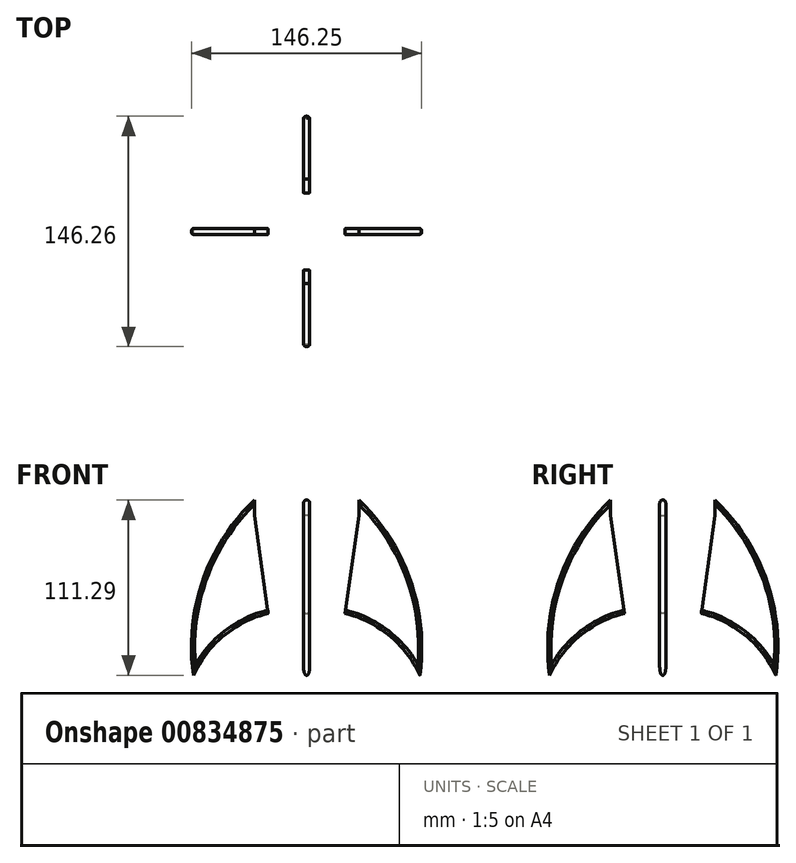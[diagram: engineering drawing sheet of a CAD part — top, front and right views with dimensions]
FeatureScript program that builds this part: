
annotation { "Feature Type Name" : "Feature", "Feature Type Description" : "" }
export const myFeature = defineFeature(function(context is Context, id is Id, definition is map)
    precondition{}
    {
        {
            var Q0;
            Q0=qCreatedBy(makeId("Front.planeOp"),FACE);
            var sketch = newSketch(context, id + "F0", { "sketchPlane" : qUnion([Q0])});
            skLineSegment(sketch, "E0", {"start": v(0, 1.98) * mm, "end": v(0, 124.8) * mm, "construction": true});
            skLineSegment(sketch, "E1.bottom", {"start": v(-9, 31.24) * mm, "end": v(9, 31.24) * mm, "construction": true});
            skLineSegment(sketch, "E1.top", {"start": v(-9, 101.24) * mm, "end": v(9, 101.24) * mm, "construction": true});
            skLineSegment(sketch, "E1.left", {"start": v(-9, 31.24) * mm, "end": v(-9, 101.24) * mm, "construction": true});
            skLineSegment(sketch, "E1.right", {"start": v(9, 31.24) * mm, "end": v(9, 101.24) * mm, "construction": true});
            skSolve(sketch);
        }
        {
            var Q0;
            Q0=qCreatedBy(makeId("Front.planeOp"),FACE);
            var sketch = newSketch(context, id + "F1", { "sketchPlane" : qUnion([Q0])});
            skLineSegment(sketch, "E2.MirrorCS", {"start": v(9.15, 101.26) * mm, "end": v(9.15, 33.17) * mm});
            skLineSegment(sketch, "E3.MirrorCS", {"start": v(33.01, 101.3) * mm, "end": v(23.86, 34.74) * mm});
            skLineSegment(sketch, "E4.MirrorCS", {"start": v(32, 101.3) * mm, "end": v(9.15, 101.26) * mm});
            skLineSegment(sketch, "E5.MirrorCS", {"start": v(32, 101.3) * mm, "end": v(32, 111.3) * mm});
            skLineSegment(sketch, "E6.MirrorCS", {"start": v(33.01, 111.3) * mm, "end": v(33.01, 101.3) * mm});
            skLineSegment(sketch, "E7.MirrorCS", {"start": v(32, 111.3) * mm, "end": v(33.01, 111.3) * mm});
            skLineSegment(sketch, "E8.MirrorCS", {"start": v(19.69, 21.09) * mm, "end": v(19.69, 34.74) * mm});
            skLineSegment(sketch, "E9.MirrorCS", {"start": v(19.69, 34.74) * mm, "end": v(23.86, 34.74) * mm});
            skLineSegment(sketch, "E10.MirrorCS", {"start": v(9.15, 33.17) * mm, "end": v(11.05, 33.17) * mm});
            skLineSegment(sketch, "E11.MirrorCS", {"start": v(11.05, 33.17) * mm, "end": v(11.05, 30.73) * mm});
            skLineSegment(sketch, "E12.MirrorCS", {"start": v(11.05, 30.73) * mm, "end": v(18.59, 21.09) * mm});
            skLineSegment(sketch, "E13.MirrorCS", {"start": v(18.59, 21.09) * mm, "end": v(19.69, 21.09) * mm});
            skLineSegment(sketch, "E14", {"start": v(12.5, 94.18) * mm, "end": v(28.58, 94.18) * mm});
            skLineSegment(sketch, "E15", {"start": v(28.58, 94.18) * mm, "end": v(21.03, 39.29) * mm});
            skLineSegment(sketch, "E16", {"start": v(21.03, 39.29) * mm, "end": v(12.3, 39.29) * mm});
            skLineSegment(sketch, "E17", {"start": v(12.3, 39.29) * mm, "end": v(12.5, 94.18) * mm});
            skSolve(sketch);
        }
        {
            var Q0;
            Q0=qCreatedBy(makeId("Front.planeOp"),FACE);
            var sketch = newSketch(context, id + "F2", { "sketchPlane" : qUnion([Q0])});
            skLineSegment(sketch, "E18", {"start": v(-19.33, 101.39) * mm, "end": v(-19.33, 106.39) * mm});
            skLineSegment(sketch, "E19", {"start": v(-19.33, 106.39) * mm, "end": v(-9.53, 106.39) * mm});
            skLineSegment(sketch, "E20", {"start": v(-9.53, 106.39) * mm, "end": v(-9.53, 166) * mm});
            skLineSegment(sketch, "E21", {"start": v(-9.53, 166) * mm, "end": v(-19.33, 166) * mm});
            skLineSegment(sketch, "E22", {"start": v(-19.33, 166) * mm, "end": v(-19.33, 172.66) * mm});
            skLineSegment(sketch, "E23", {"start": v(-19.33, 172.66) * mm, "end": v(-7.98, 172.66) * mm});
            skLineSegment(sketch, "E24", {"start": v(-7.98, 172.66) * mm, "end": v(-7.98, 171.53) * mm});
            skLineSegment(sketch, "E25", {"start": v(-7.98, 171.53) * mm, "end": v(-9, 171.53) * mm});
            skLineSegment(sketch, "E26", {"start": v(-9, 171.53) * mm, "end": v(-9, 104.37) * mm});
            skArc(sketch, "E27", {"start": v(-9, 104.37) * mm, "mid": v(-10.81, 103.2) * mm, "end": v(-11.96, 101.39) * mm});
            skLineSegment(sketch, "E28", {"start": v(-11.96, 101.39) * mm, "end": v(-19.33, 101.39) * mm});
            skSolve(sketch);
        }
        {
            var Q0;
            Q0=sQuery(id+"F1.wireOp",EDGE,"E2.MirrorCS");
            var Q1;
            Q1=sQuery(id+"F1.wireOp",EDGE,"E4.MirrorCS");
            var Q2;
            Q2=sQuery(id+"F1.wireOp",EDGE,"E6.MirrorCS");
            var Q3;
            Q3=sQuery(id+"F1.wireOp",EDGE,"E3.MirrorCS");
            var Q4;
            Q4=sQuery(id+"F1.wireOp",EDGE,"E5.MirrorCS");
            var Q5;
            Q5=sQuery(id+"F1.wireOp",EDGE,"E9.MirrorCS");
            var Q6;
            Q6=sQuery(id+"F1.wireOp",EDGE,"E11.MirrorCS");
            var Q7;
            Q7=sQuery(id+"F1.wireOp",EDGE,"E7.MirrorCS");
            var Q8;
            Q8=sQuery(id+"F1.wireOp",EDGE,"E10.MirrorCS");
            var Q9;
            Q9=sQuery(id+"F1.wireOp",EDGE,"E8.MirrorCS");
            var Q10;
            Q10=sQuery(id+"F1.wireOp",EDGE,"E12.MirrorCS");
            var Q11;
            Q11=sQuery(id+"F1.wireOp",EDGE,"E13.MirrorCS");
            var Q12;
            Q12 = qConstructionFilter(qBodyType(qCreatedBy(id + "F2" ,EDGE), BodyType.WIRE), ConstructionObject.NO);
            var Q13;
            Q13=sQuery(id+"F0.wireOp",EDGE,"E0");
            revolve(context, id + "F3", {"bodyType" : ToolBodyType.SURFACE, "surfaceOperationType" : NewSurfaceOperationType.NEW, "surfaceEntities" : qUnion([Q0, Q1, Q2, Q3, Q4, Q5, Q6, Q7, Q8, Q9, Q10, Q11, Q12]), "axis" : qUnion([Q13]), "revolveType" : RevolveType.FULL});
        }
        {
            var Q0;
            Q0=makeQuery(id+"F3.opRevolve","SWEPT_EDGE",EDGE,{"disambiguationData":[OSD([sQuery(id+"F1.wireOp",VERTEX,"E4.MirrorCS.end")])]});
            var Q1;
            Q1=makeQuery(id+"F3.opRevolve","SWEPT_EDGE",EDGE,{"disambiguationData":[OSD([sQuery(id+"F1.wireOp",VERTEX,"E13.MirrorCS.end")])]});
            var Q2;
            Q2=makeQuery(id+"F3.opRevolve","SWEPT_EDGE",EDGE,{"disambiguationData":[OSD([sQuery(id+"F1.wireOp",VERTEX,"E10.MirrorCS.start")])]});
            fillet(context, id + "F4", {"entities" : qUnion([Q0, Q1, Q2]), "radius" : 5 * mm, "tangentPropagation" : true, "allowEdgeOverflow" : false});
        }
        {
            var Q0;
            Q0=qCreatedBy(makeId("Front.planeOp"),FACE);
            var sketch = newSketch(context, id + "F5", { "sketchPlane" : qUnion([Q0])});
            skArc(sketch, "E29", {"start": v(-24.4, 39.36) * mm, "mid": v(-52.64, 25.1) * mm, "end": v(-71.9, 0) * mm});
            skArc(sketch, "E30", {"start": v(-33.16, 111.3) * mm, "mid": v(-65.94, 60.31) * mm, "end": v(-71.9, 0) * mm});
            skLineSegment(sketch, "E31", {"start": v(-33.16, 111.3) * mm, "end": v(-33.16, 101.44) * mm});
            skLineSegment(sketch, "E32", {"start": v(-33.16, 101.44) * mm, "end": v(-24.4, 39.36) * mm});
            skArc(sketch, "E33.MirrorCS", {"start": v(33.16, 111.3) * mm, "mid": v(65.94, 60.31) * mm, "end": v(71.9, 0) * mm});
            skArc(sketch, "E34.MirrorCS", {"start": v(24.4, 39.36) * mm, "mid": v(52.64, 25.1) * mm, "end": v(71.9, 0) * mm});
            skLineSegment(sketch, "E35.MirrorCS", {"start": v(33.16, 101.44) * mm, "end": v(24.4, 39.36) * mm});
            skLineSegment(sketch, "E36.MirrorCS", {"start": v(33.16, 111.3) * mm, "end": v(33.16, 101.44) * mm});
            skSolve(sketch);
        }
        {
            var Q0;
            Q0=qSketchRegion(id+"F5",true);
            extrude(context, id + "F6", {"entities" : qUnion([Q0]), "depth" : 2 * mm, "offsetDistance" : 25 * mm, "hasSecondDirection" : true, "secondDirectionOppositeDirection" : true, "secondDirectionDepth" : 2 * mm});
        }
        {
            var Q0;
            Q0=qCreatedBy(makeId("Right.planeOp"),FACE);
            var sketch = newSketch(context, id + "F7", { "sketchPlane" : qUnion([Q0])});
            skArc(sketch, "E37", {"start": v(-24.36, 39.36) * mm, "mid": v(-52.6, 25.1) * mm, "end": v(-71.86, 0) * mm});
            skArc(sketch, "E38", {"start": v(-33.12, 111.3) * mm, "mid": v(-65.9, 60.31) * mm, "end": v(-71.86, 0) * mm});
            skLineSegment(sketch, "E39", {"start": v(-33.12, 111.3) * mm, "end": v(-33.12, 101.44) * mm});
            skLineSegment(sketch, "E40", {"start": v(-33.12, 101.44) * mm, "end": v(-24.36, 39.36) * mm});
            skArc(sketch, "E41.MirrorCS", {"start": v(33.2, 111.3) * mm, "mid": v(65.98, 60.31) * mm, "end": v(71.94, 0) * mm});
            skArc(sketch, "E42.MirrorCS", {"start": v(24.44, 39.36) * mm, "mid": v(52.69, 25.1) * mm, "end": v(71.94, 0) * mm});
            skLineSegment(sketch, "E43.MirrorCS", {"start": v(33.2, 101.44) * mm, "end": v(24.44, 39.36) * mm});
            skLineSegment(sketch, "E44.MirrorCS", {"start": v(33.2, 111.3) * mm, "end": v(33.2, 101.44) * mm});
            skSolve(sketch);
        }
        {
            var Q0;
            Q0=qSketchRegion(id+"F7",true);
            extrude(context, id + "F8", {"entities" : qUnion([Q0]), "depth" : 2 * mm, "offsetDistance" : 25 * mm, "hasSecondDirection" : true, "secondDirectionOppositeDirection" : true, "secondDirectionDepth" : 2 * mm});
        }
        {
            var Q0;
            Q0=makeQuery(id+"F6.opExtrude","CAP_EDGE",EDGE,{"disambiguationData":[OSD([sQuery(id+"F5.wireOp",EDGE,"E33.MirrorCS")])],"isStart":false});
            var Q1;
            Q1=makeQuery(id+"F6.opExtrude","CAP_EDGE",EDGE,{"disambiguationData":[OSD([sQuery(id+"F5.wireOp",EDGE,"E33.MirrorCS")])],"isStart":true});
            var Q2;
            Q2=makeQuery(id+"F6.opExtrude","CAP_EDGE",EDGE,{"disambiguationData":[OSD([sQuery(id+"F5.wireOp",EDGE,"E34.MirrorCS")])],"isStart":false});
            var Q3;
            Q3=makeQuery(id+"F6.opExtrude","CAP_EDGE",EDGE,{"disambiguationData":[OSD([sQuery(id+"F5.wireOp",EDGE,"E34.MirrorCS")])],"isStart":true});
            var Q4;
            Q4=makeQuery(id+"F6.opExtrude","CAP_EDGE",EDGE,{"disambiguationData":[OSD([sQuery(id+"F5.wireOp",EDGE,"E30")])],"isStart":false});
            var Q5;
            Q5=makeQuery(id+"F6.opExtrude","CAP_EDGE",EDGE,{"disambiguationData":[OSD([sQuery(id+"F5.wireOp",EDGE,"E30")])],"isStart":true});
            var Q6;
            Q6=makeQuery(id+"F6.opExtrude","CAP_EDGE",EDGE,{"disambiguationData":[OSD([sQuery(id+"F5.wireOp",EDGE,"E29")])],"isStart":false});
            var Q7;
            Q7=makeQuery(id+"F6.opExtrude","CAP_EDGE",EDGE,{"disambiguationData":[OSD([sQuery(id+"F5.wireOp",EDGE,"E29")])],"isStart":true});
            var Q8;
            Q8=makeQuery(id+"F8.opExtrude","CAP_EDGE",EDGE,{"disambiguationData":[OSD([sQuery(id+"F7.wireOp",EDGE,"E41.MirrorCS")])],"isStart":false});
            var Q9;
            Q9=makeQuery(id+"F8.opExtrude","CAP_EDGE",EDGE,{"disambiguationData":[OSD([sQuery(id+"F7.wireOp",EDGE,"E42.MirrorCS")])],"isStart":false});
            var Q10;
            Q10=makeQuery(id+"F8.opExtrude","CAP_EDGE",EDGE,{"disambiguationData":[OSD([sQuery(id+"F7.wireOp",EDGE,"E41.MirrorCS")])],"isStart":true});
            var Q11;
            Q11=makeQuery(id+"F8.opExtrude","CAP_EDGE",EDGE,{"disambiguationData":[OSD([sQuery(id+"F7.wireOp",EDGE,"E42.MirrorCS")])],"isStart":true});
            fillet(context, id + "F9", {"entities" : qUnion([Q0, Q1, Q2, Q3, Q4, Q5, Q6, Q7, Q8, Q9, Q10, Q11]), "radius" : 2 * mm, "tangentPropagation" : true, "rho" : 0.5, "crossSection" : FilletCrossSection.CONIC, "allowEdgeOverflow" : false});
        }
        {
            var Q0;
            Q0=makeQuery(id+"F8.opExtrude","CAP_EDGE",EDGE,{"disambiguationData":[OSD([sQuery(id+"F7.wireOp",EDGE,"E38")])],"isStart":true});
            var Q1;
            Q1=makeQuery(id+"F8.opExtrude","CAP_EDGE",EDGE,{"disambiguationData":[OSD([sQuery(id+"F7.wireOp",EDGE,"E38")])],"isStart":false});
            var Q2;
            Q2=makeQuery(id+"F8.opExtrude","CAP_EDGE",EDGE,{"disambiguationData":[OSD([sQuery(id+"F7.wireOp",EDGE,"E37")])],"isStart":true});
            var Q3;
            Q3=makeQuery(id+"F8.opExtrude","CAP_EDGE",EDGE,{"disambiguationData":[OSD([sQuery(id+"F7.wireOp",EDGE,"E37")])],"isStart":false});
            fillet(context, id + "F10", {"entities" : qUnion([Q0, Q1, Q2, Q3]), "radius" : 2 * mm, "tangentPropagation" : true, "rho" : 0.5, "crossSection" : FilletCrossSection.CONIC, "allowEdgeOverflow" : false});
        }
    });
